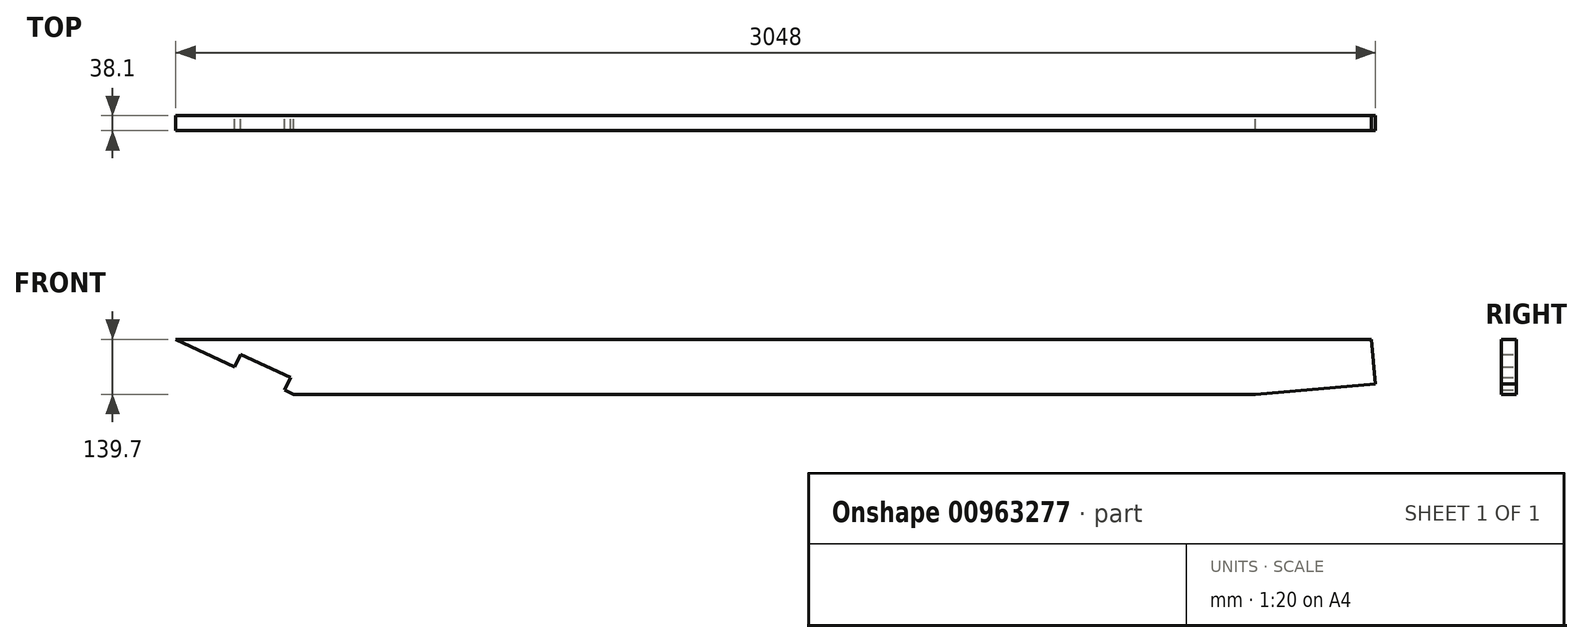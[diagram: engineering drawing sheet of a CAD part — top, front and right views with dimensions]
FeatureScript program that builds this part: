
annotation { "Feature Type Name" : "Feature", "Feature Type Description" : "" }
export const myFeature = defineFeature(function(context is Context, id is Id, definition is map)
    precondition{}
    {
        {
            var Q0;
            Q0=qCreatedBy(makeId("Front.planeOp"),FACE);
            var sketch = newSketch(context, id + "F0", { "sketchPlane" : qUnion([Q0])});
            skLineSegment(sketch, "E0.bottom", {"start": v(0, 0) * mm, "end": v(3048, 0) * mm});
            skLineSegment(sketch, "E0.top", {"start": v(0, 139.7) * mm, "end": v(3048, 139.7) * mm});
            skLineSegment(sketch, "E0.left", {"start": v(0, 0) * mm, "end": v(0, 139.7) * mm});
            skLineSegment(sketch, "E0.right", {"start": v(3048, 0) * mm, "end": v(3048, 139.7) * mm});
            skSolve(sketch);
        }
        {
            var Q0;
            Q0=makeQuery(id+"F0.imprint","IMPRINT",FACE,{"disambiguationData":[TD([[makeQuery(id+"F0.imprint","IMPRINT",EDGE,{"derivedFrom":sQuery(id+"F0.wireOp",EDGE,"E0.bottom")}),1.0]])]});
            extrude(context, id + "F1", {"entities" : qUnion([Q0]), "depth" : 38.1 * mm, "offsetDistance" : 25.4 * mm});
        }
        {
            var Q0;
            Q0=qCreatedBy(makeId("Front.planeOp"),FACE);
            var sketch = newSketch(context, id + "F2", { "sketchPlane" : qUnion([Q0])});
            skLineSegment(sketch, "E1", {"start": v(0, 139.7) * mm, "end": v(149.96, 69.77) * mm});
            skLineSegment(sketch, "E2", {"start": v(299.59, 0) * mm, "end": v(0, 0) * mm});
            skLineSegment(sketch, "E3", {"start": v(0, 0) * mm, "end": v(0, 139.7) * mm});
            skLineSegment(sketch, "E4", {"start": v(3048, 26.67) * mm, "end": v(2743.2, 0) * mm});
            skLineSegment(sketch, "E5", {"start": v(2743.2, 0) * mm, "end": v(3048, 0) * mm});
            skLineSegment(sketch, "E6", {"start": v(3048, 0) * mm, "end": v(3048, 26.67) * mm});
            skLineSegment(sketch, "E7", {"start": v(276.57, 10.73) * mm, "end": v(291.33, 42.39) * mm});
            skLineSegment(sketch, "E8", {"start": v(291.33, 42.39) * mm, "end": v(164.72, 101.43) * mm});
            skLineSegment(sketch, "E9", {"start": v(164.72, 101.43) * mm, "end": v(149.96, 69.77) * mm});
            skLineSegment(sketch, "E10.trimOffspring", {"start": v(276.57, 10.73) * mm, "end": v(299.59, 0) * mm});
            skSolve(sketch);
        }
        {
            var Q0;
            Q0 = qSketchRegion(id + "F2", true);
            extrude(context, id + "F3", {"entities" : qUnion([Q0]), "operationType" : NewBodyOperationType.REMOVE, "endBound" : BoundingType.THROUGH_ALL, "depth" : 25.4 * mm, "offsetDistance" : 25.4 * mm});
        }
        {
            var Q0;
            Q0=makeQuery(id+"F1.opExtrude","CAP_FACE",FACE,{"disambiguationData":[OSD([sQuery(id+"F0.wireOp",EDGE,"E0.bottom"),sQuery(id+"F0.wireOp",EDGE,"E0.top"),sQuery(id+"F0.wireOp",EDGE,"E0.left"),sQuery(id+"F0.wireOp",EDGE,"E0.right")])],"isStart":false});
            var sketch = newSketch(context, id + "F4", { "sketchPlane" : qUnion([Q0])});
            skLineSegment(sketch, "E11", {"start": v(3048, 26.67) * mm, "end": v(3048, 139.7) * mm});
            skLineSegment(sketch, "E12", {"start": v(3048, 139.7) * mm, "end": v(3038.11, 139.7) * mm});
            skLineSegment(sketch, "E13", {"start": v(3038.11, 139.7) * mm, "end": v(3048, 26.67) * mm});
            skSolve(sketch);
        }
        {
            var Q0;
            Q0=makeQuery(id+"F4.imprint","IMPRINT",FACE,{"disambiguationData":[TD([[makeQuery(id+"F4.imprint","IMPRINT",EDGE,{"derivedFrom":sQuery(id+"F4.wireOp",EDGE,"E11")}),1.0]])]});
            extrude(context, id + "F5", {"entities" : qUnion([Q0]), "operationType" : NewBodyOperationType.REMOVE, "oppositeDirection" : true, "depth" : 38.1 * mm, "offsetDistance" : 25.4 * mm});
        }
    });
